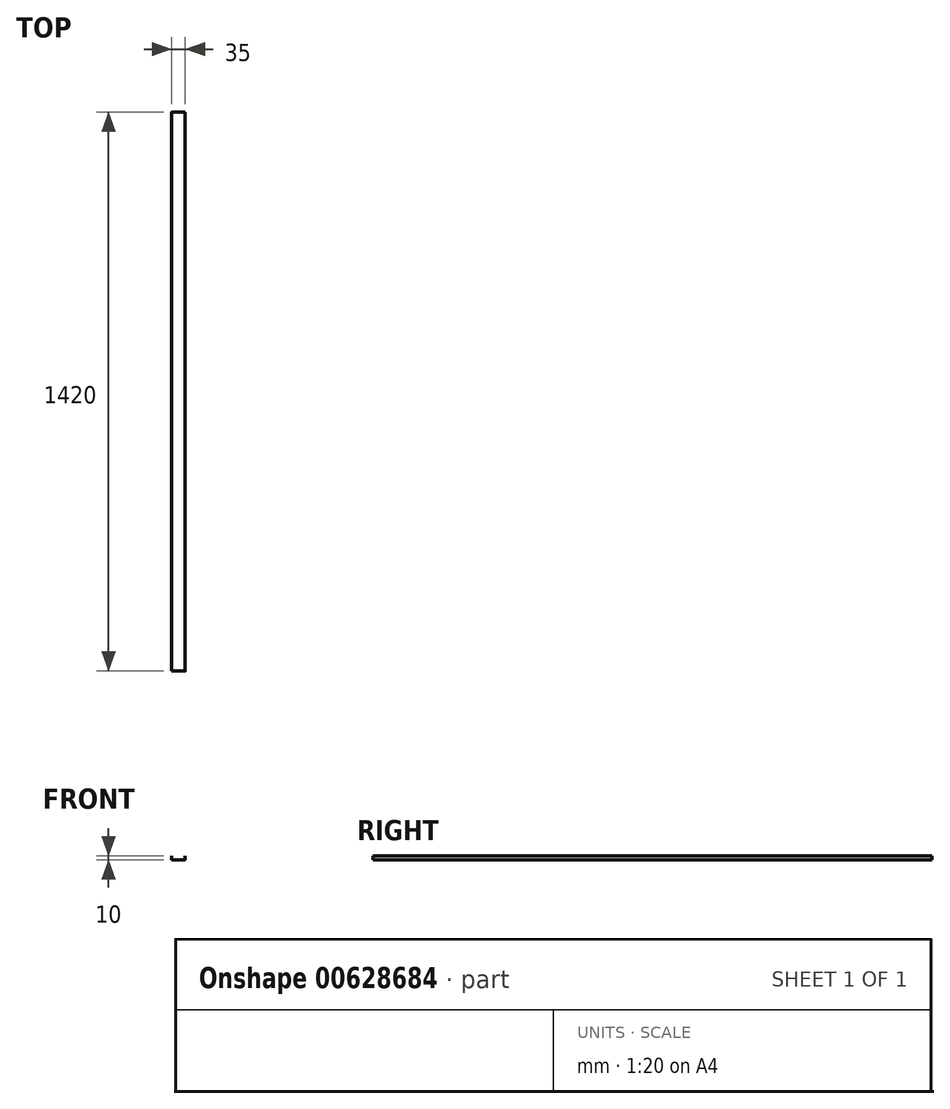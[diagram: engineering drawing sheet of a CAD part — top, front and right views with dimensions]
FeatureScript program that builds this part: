
annotation { "Feature Type Name" : "Feature", "Feature Type Description" : "" }
export const myFeature = defineFeature(function(context is Context, id is Id, definition is map)
    precondition{}
    {
        {
            var Q0;
            Q0=qCreatedBy(makeId("Front.planeOp"),FACE);
            var sketch = newSketch(context, id + "F0", { "sketchPlane" : qUnion([Q0])});
            skLineSegment(sketch, "E0", {"start": v(0, 0) * mm, "end": v(0, -9.25) * mm});
            skLineSegment(sketch, "E1", {"start": v(0.75, -10) * mm, "end": v(34.25, -10) * mm});
            skLineSegment(sketch, "E2", {"start": v(35, -9.25) * mm, "end": v(35, 0) * mm});
            skLineSegment(sketch, "E3", {"start": v(35, 0) * mm, "end": v(34.5, 0) * mm});
            skLineSegment(sketch, "E4", {"start": v(34.5, 0) * mm, "end": v(34.5, -9) * mm});
            skLineSegment(sketch, "E5", {"start": v(34, -9.5) * mm, "end": v(1, -9.5) * mm});
            skLineSegment(sketch, "E6", {"start": v(0.5, -9) * mm, "end": v(0.5, 0) * mm});
            skLineSegment(sketch, "E7", {"start": v(0.5, 0) * mm, "end": v(0, 0) * mm});
            skPoint(sketch, "E8.visualSharp", {"position": v(0.5, -9.5) * mm});
            skArc(sketch, "E8.filletArc", {"start": v(0.5, -9) * mm, "mid": v(0.65, -9.35) * mm, "end": v(1, -9.5) * mm});
            skPoint(sketch, "E9.visualSharp", {"position": v(0, -10) * mm});
            skArc(sketch, "E9.filletArc", {"start": v(0, -9.25) * mm, "mid": v(0.22, -9.78) * mm, "end": v(0.75, -10) * mm});
            skPoint(sketch, "E10.visualSharp", {"position": v(34.5, -9.5) * mm});
            skArc(sketch, "E10.filletArc", {"start": v(34, -9.5) * mm, "mid": v(34.35, -9.35) * mm, "end": v(34.5, -9) * mm});
            skPoint(sketch, "E11.visualSharp", {"position": v(35, -10) * mm});
            skArc(sketch, "E11.filletArc", {"start": v(34.25, -10) * mm, "mid": v(34.78, -9.78) * mm, "end": v(35, -9.25) * mm});
            skSolve(sketch);
        }
        {
            var Q0;
            Q0=makeQuery(id+"F0.imprint","IMPRINT",FACE,{"disambiguationData":[TD([[makeQuery(id+"F0.imprint","IMPRINT",EDGE,{"derivedFrom":sQuery(id+"F0.wireOp",EDGE,"E0")}),1.0]])]});
            extrude(context, id + "F1", {"entities" : qUnion([Q0]), "depth" : 1420 * mm, "offsetDistance" : 25 * mm});
        }
    });
